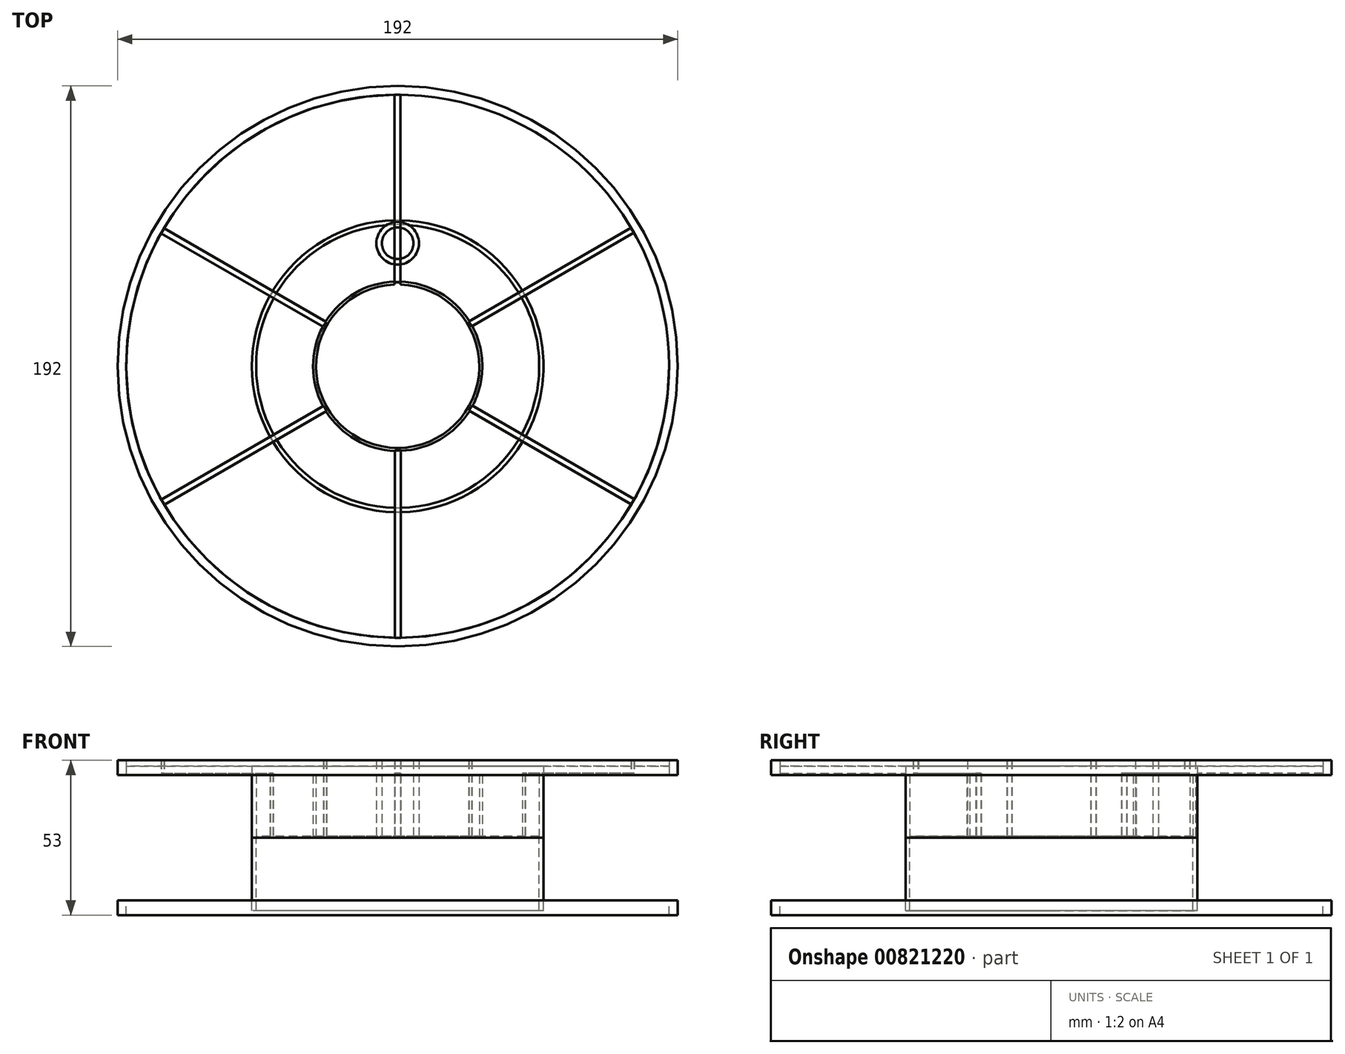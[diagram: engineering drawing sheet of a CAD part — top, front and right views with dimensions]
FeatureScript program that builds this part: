
annotation { "Feature Type Name" : "Feature", "Feature Type Description" : "" }
export const myFeature = defineFeature(function(context is Context, id is Id, definition is map)
    precondition{}
    {
        {
            var Q0;
            Q0=qCreatedBy(makeId("Top.planeOp"),FACE);
            var sketch = newSketch(context, id + "F0", { "sketchPlane" : qUnion([Q0])});
            skCircle(sketch, "E0", {"center": v(0, 0) * mm, "radius": 28 * mm});
            skCircle(sketch, "E1", {"center": v(0, 0) * mm, "radius": 93 * mm});
            skCircle(sketch, "E2", {"center": v(0, 0) * mm, "radius": 48.5 * mm});
            skCircle(sketch, "E3", {"center": v(0, 0) * mm, "radius": 96 * mm});
            skCircle(sketch, "E4", {"center": v(0, 0) * mm, "radius": 50 * mm});
            skCircle(sketch, "E5", {"center": v(0, 0) * mm, "radius": 29 * mm});
            skSolve(sketch);
        }
        {
            var Q0;
            Q0=makeQuery(id+"F0.imprint","IMPRINT",FACE,{"disambiguationData":[TD([[makeQuery(id+"F0.imprint","IMPRINT",EDGE,{"derivedFrom":sQuery(id+"F0.wireOp",EDGE,"E0")}),-1.0]])]});
            var Q1;
            Q1=makeQuery(id+"F0.imprint","IMPRINT",FACE,{"disambiguationData":[TD([[makeQuery(id+"F0.imprint","IMPRINT",EDGE,{"derivedFrom":sQuery(id+"F0.wireOp",EDGE,"E2")}),-1.0]])]});
            extrude(context, id + "F1", {"entities" : qUnion([Q0, Q1]), "depth" : 21.5 * mm, "offsetDistance" : 25 * mm});
        }
        {
            var Q0;
            Q0=makeQuery(id+"F0.imprint","IMPRINT",FACE,{"disambiguationData":[TD([[makeQuery(id+"F0.imprint","IMPRINT",EDGE,{"derivedFrom":sQuery(id+"F0.wireOp",EDGE,"E2")}),1.0]])]});
            extrude(context, id + "F2", {"entities" : qUnion([Q0]), "depth" : .5 * mm, "offsetDistance" : 25 * mm});
        }
        {
            var Q0;
            Q0=makeQuery(id+"F0.imprint","IMPRINT",FACE,{"disambiguationData":[TD([[makeQuery(id+"F0.imprint","IMPRINT",EDGE,{"derivedFrom":sQuery(id+"F0.wireOp",EDGE,"E1")}),-1.0]])]});
            extrude(context, id + "F3", {"entities" : qUnion([Q0]), "depth" : 26.5 * mm, "offsetDistance" : 25 * mm});
        }
        {
            var Q0;
            Q0=makeQuery(id+"F0.imprint","IMPRINT",FACE,{"disambiguationData":[TD([[makeQuery(id+"F0.imprint","IMPRINT",EDGE,{"derivedFrom":sQuery(id+"F0.wireOp",EDGE,"E1")}),1.0]])]});
            extrude(context, id + "F4", {"entities" : qUnion([Q0]), "depth" : 24.5 * mm, "offsetDistance" : 25 * mm});
        }
        {
            var Q0;
            Q0=makeQuery(id+"F0.imprint","IMPRINT",FACE,{"disambiguationData":[TD([[makeQuery(id+"F0.imprint","IMPRINT",EDGE,{"derivedFrom":sQuery(id+"F0.wireOp",EDGE,"E1")}),-1.0]])]});
            var Q1;
            Q1=makeQuery(id+"F0.imprint","IMPRINT",FACE,{"disambiguationData":[TD([[makeQuery(id+"F0.imprint","IMPRINT",EDGE,{"derivedFrom":sQuery(id+"F0.wireOp",EDGE,"E1")}),1.0]])]});
            extrude(context, id + "F5", {"entities" : qUnion([Q0, Q1]), "operationType" : NewBodyOperationType.REMOVE, "depth" : 21.5 * mm, "offsetDistance" : 25 * mm});
        }
        {
            var Q0;
            Q0=makeQuery(id+"F0.imprint","IMPRINT",FACE,{"disambiguationData":[TD([[makeQuery(id+"F0.imprint","IMPRINT",EDGE,{"derivedFrom":sQuery(id+"F0.wireOp",EDGE,"E1")}),1.0]])]});
            extrude(context, id + "F6", {"entities" : qUnion([Q0]), "operationType" : NewBodyOperationType.REMOVE, "depth" : 21.5 * mm, "offsetDistance" : 25 * mm});
        }
        {
            var Q0;
            Q0=qCreatedBy(makeId("Top.planeOp"),FACE);
            var sketch = newSketch(context, id + "F7", { "sketchPlane" : qUnion([Q0])});
            skLineSegment(sketch, "E6.bottom", {"start": v(-1.08, 0) * mm, "end": v(0.92, 0) * mm});
            skLineSegment(sketch, "E6.top", {"start": v(-1.08, 93) * mm, "end": v(0.92, 93) * mm});
            skLineSegment(sketch, "E6.left", {"start": v(-1.08, 0) * mm, "end": v(-1.08, 93) * mm});
            skLineSegment(sketch, "E6.right", {"start": v(0.92, 0) * mm, "end": v(0.92, 93) * mm});
            skLineSegment(sketch, "E7", {"start": v(-1.08, 28.7) * mm, "end": v(0.92, 28.7) * mm});
            skSolve(sketch);
        }
        {
            var Q0;
            Q0 = qSketchRegion(id + "F7", true);
            extrude(context, id + "F8", {"entities" : qUnion([Q0]), "depth" : 26.5 * mm, "offsetDistance" : 25 * mm});
        }
        {
            var Q0;
            Q0=makeQuery(id+"F8.opExtrude","SWEPT_FACE",FACE,{"disambiguationData":[OSD([sQuery(id+"F7.wireOp",EDGE,"E6.left")])]});
            var sketch = newSketch(context, id + "F9", { "sketchPlane" : qUnion([Q0])});
            skLineSegment(sketch, "E8", {"start": v(-93, 22.05) * mm, "end": v(-49.9, 22.05) * mm});
            skLineSegment(sketch, "E9", {"start": v(-49.9, 22.05) * mm, "end": v(-49.9, 0) * mm});
            skLineSegment(sketch, "E10", {"start": v(-28.76, 26.5) * mm, "end": v(-28.76, 0) * mm});
            skSolve(sketch);
        }
        {
            var Q0;
            {var subQ0=sQuery(id+"F9.wireOp",EDGE,"E8");Q0=makeQuery(id+"F9.imprint","IMPRINT",FACE,{"disambiguationData":[TD([[makeQuery(id+"F9.imprint","IMPRINT",EDGE,{"derivedFrom":subQ0}),-1.0]])]});}
            var Q1;
            {var subQ0=sQuery(id+"F9.wireOp",EDGE,"E10");Q1=makeQuery(id+"F9.imprint","IMPRINT",FACE,{"disambiguationData":[TD([[makeQuery(id+"F9.imprint","IMPRINT",EDGE,{"derivedFrom":subQ0}),1.0]])]});}
            extrude(context, id + "F10", {"entities" : qUnion([Q0, Q1]), "operationType" : NewBodyOperationType.REMOVE, "oppositeDirection" : true, "depth" : 2 * mm, "offsetDistance" : 25 * mm});
        }
        {
            var Q0;
            Q0=qCreatedBy(makeId("Front.planeOp"),FACE);
            var sketch = newSketch(context, id + "F11", { "sketchPlane" : qUnion([Q0])});
            skLineSegment(sketch, "E11", {"start": v(0, 0) * mm, "end": v(0, 15.3) * mm});
            skSolve(sketch);
        }
        {
            var Q0;
            Q0=makeQuery(id+"F8.opExtrude","SWEPT_BODY",BODY,{"disambiguationData":[OSD([sQuery(id+"F7.wireOp",EDGE,"E6.bottom"),sQuery(id+"F7.wireOp",EDGE,"E6.top"),sQuery(id+"F7.wireOp",EDGE,"E6.left"),sQuery(id+"F7.wireOp",EDGE,"E6.right")])]});
            var Q1;
            Q1=sQuery(id+"F11.wireOp",EDGE,"E11");
            circularPattern(context, id + "F12", {"entities" : qUnion([Q0]), "axis" : qUnion([Q1]), "angle" : 360 * degree, "instanceCount" : 6, "equalSpace" : true});
        }
        {
            var Q0;
            Q0=qCreatedBy(makeId("Top.planeOp"),FACE);
            var sketch = newSketch(context, id + "F13", { "sketchPlane" : qUnion([Q0])});
            skCircle(sketch, "E12", {"center": v(0, 42.1) * mm, "radius": 7.3 * mm});
            skCircle(sketch, "E13", {"center": v(0, 42.1) * mm, "radius": 5.42 * mm});
            skSolve(sketch);
        }
        {
            var Q0;
            Q0 = qSketchRegion(id + "F13", true);
            extrude(context, id + "F14", {"entities" : qUnion([Q0]), "depth" : 26.5 * mm, "offsetDistance" : 25 * mm});
        }
        {
            var Q0;
            Q0=makeQuery(id+"F3.opExtrude","SWEPT_BODY",BODY,{"disambiguationData":[OSD([sQuery(id+"F0.wireOp",EDGE,"E1"),sQuery(id+"F0.wireOp",EDGE,"E3")])]});
            var Q1;
            Q1=qCreatedBy(makeId("Top.planeOp"),FACE);
            mirror(context, id + "F15", {"entities" : qUnion([Q0]), "mirrorPlane" : qUnion([Q1])});
        }
        {
            var Q0;
            Q0=makeQuery(id+"F0.imprint","IMPRINT",FACE,{"disambiguationData":[TD([[makeQuery(id+"F0.imprint","IMPRINT",EDGE,{"derivedFrom":sQuery(id+"F0.wireOp",EDGE,"E2")}),-1.0]])]});
            extrude(context, id + "F16", {"entities" : qUnion([Q0]), "oppositeDirection" : true, "depth" : 25 * mm, "offsetDistance" : 25 * mm});
        }
    });
